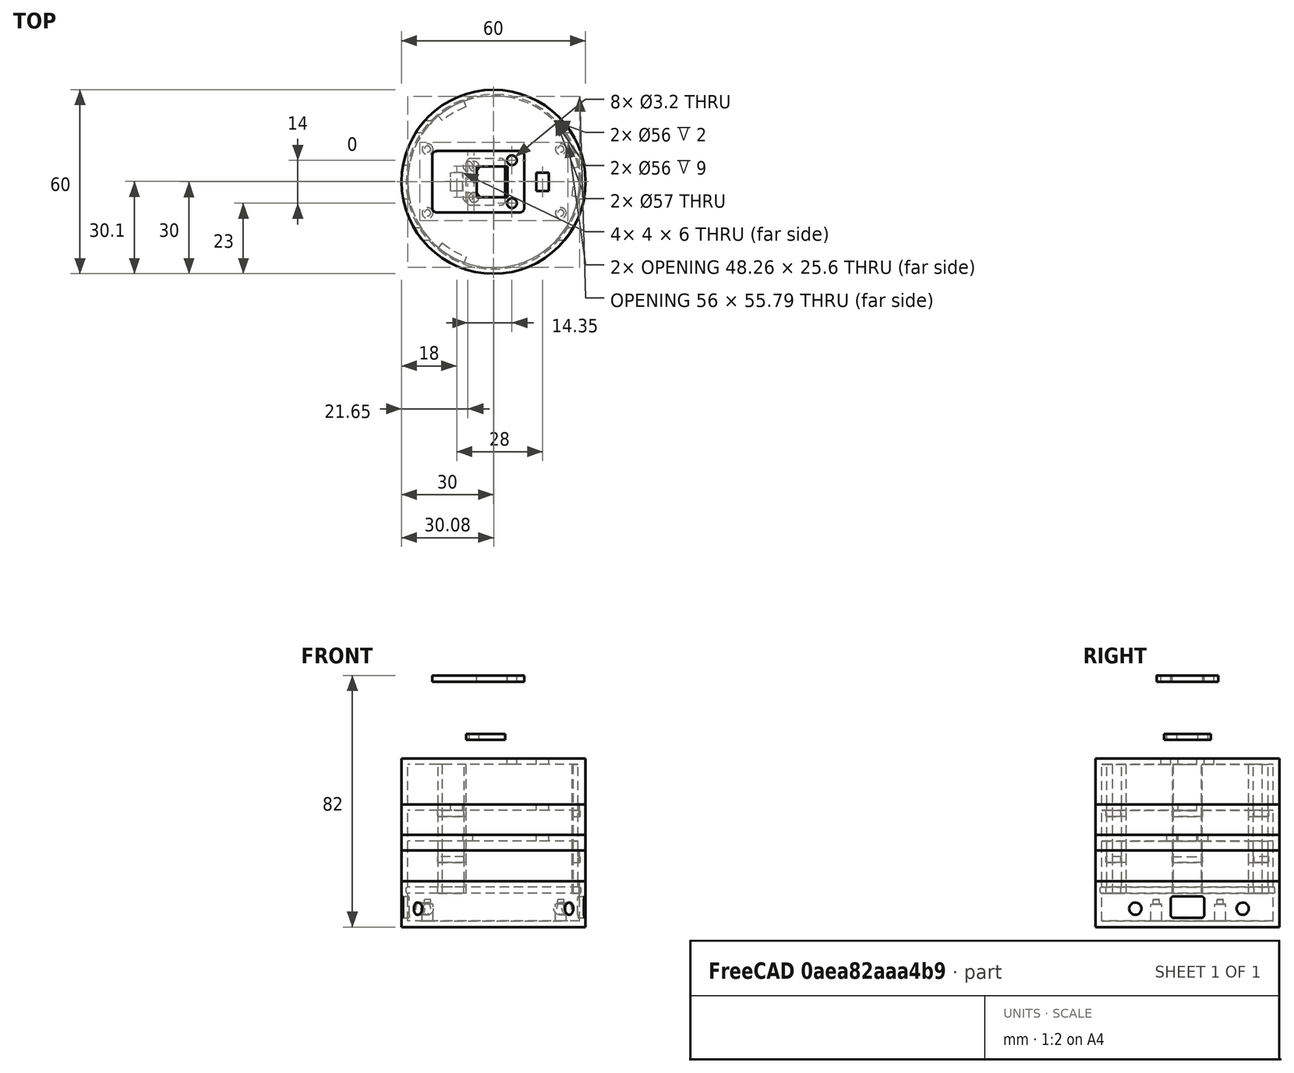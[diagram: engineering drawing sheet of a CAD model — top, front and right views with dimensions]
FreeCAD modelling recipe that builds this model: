
FCSTD DOCUMENT  (FreeCAD 0.18R16146 (Git))
Label: Esp8266_NodeMCU_SensorHousing
License: All rights reserved
LicenseURL: http://en.wikipedia.org/wiki/All_rights_reserved
objects: Part::Cylinder×19, Part::Cut×18, Part::Box×10, Part::MultiFuse×10, Part::Fillet×6, Part::Fuse×4, App::DocumentObjectGroup×3
note: 67 computed .brp shape members not serialized (recipe doc carries the construction recipe); baked Part::Feature solids carry a one-line shape summary decoded from their .brp

FEATURE [Part::Box] Box  label="ESP8266MountingBlock"
  AttacherType = Attacher::AttachEngine3D
  Height = 2
  Length = 48.26
  Width = 25.6
FEATURE [Part::Cylinder] Cylinder  label="DistancePieceLowerLeft"
  Angle = 360
  AttacherType = Attacher::AttachEngine3D
  Height = 7.5
  Placement = pos=(2.54,2.54,0) rot=(0,0,1;0rad)
  Radius = 1.75
FEATURE [Part::Cylinder] Cylinder001  label="MountPieceLowerLeft"
  Angle = 360
  AttacherType = Attacher::AttachEngine3D
  Height = 9
  Placement = pos=(2.54,2.54,0) rot=(0,0,1;0rad)
  Radius = 1
FEATURE [Part::Fuse] Fusion  label="LowerLeftMount"
  Base = -> Cylinder
  Tool = -> Cylinder001
FEATURE [Part::Fuse] Fusion001  label="LowerRightMount"
  Base = -> Cylinder
  Placement = pos=(43.434,0,0) rot=(0,0,1;0rad)
  Tool = -> Cylinder001
FEATURE [Part::Fuse] Fusion002  label="UpperLeftMount"
  Base = -> Cylinder
  Placement = pos=(0,20.828,0) rot=(0,0,1;0rad)
  Tool = -> Cylinder001
FEATURE [Part::Fuse] Fusion003  label="UpperRightMount"
  Base = -> Cylinder
  Placement = pos=(43.434,20.828,0) rot=(0,0,1;0rad)
  Tool = -> Cylinder001
FEATURE [Part::Fillet] Fillet
  Base = -> Box
  Edges = 4 edges r=2: [Edge1,Edge3,Edge5,Edge7]
FEATURE [Part::MultiFuse] Fusion004  label="ESP8266_bracket"
  Placement = pos=(-24.05,-12.7,0) rot=(0,0,1;0rad)
  Shapes = -> [Fusion002,Fusion003,Fillet,Fusion001,Fusion]
FEATURE [Part::Cylinder] Cylinder002  label="LowerHousingOuter"
  Angle = 360
  AttacherType = Attacher::AttachEngine3D
  Height = 15
  Radius = 30
FEATURE [Part::Cylinder] Cylinder003  label="LowerHousingInner"
  Angle = 360
  AttacherType = Attacher::AttachEngine3D
  Height = 15
  Placement = pos=(0,0,2) rot=(0,0,1;0rad)
  Radius = 28
FEATURE [Part::Cut] Cut  label="LowerHousing"
  Base = -> Cylinder002
  Tool = -> Cylinder003
FEATURE [Part::Cylinder] Cylinder004  label="UpperHousingOuter"
  Angle = 360
  AttacherType = Attacher::AttachEngine3D
  Height = 15
  Placement = pos=(0,0,15) rot=(0,0,1;0rad)
  Radius = 30
FEATURE [Part::Cylinder] Cylinder005  label="UpperHousingInner"
  Angle = 360
  AttacherType = Attacher::AttachEngine3D
  Height = 13
  Placement = pos=(0,0,15) rot=(0,0,1;0rad)
  Radius = 28
FEATURE [Part::Cylinder] Cylinder006  label="LowerHousingNotch"
  Angle = 360
  AttacherType = Attacher::AttachEngine3D
  Height = 2
  Placement = pos=(0,0,11) rot=(0,0,1;0rad)
  Radius = 28.5
FEATURE [Part::Cut] Cut002  label="UpperHousing"
  Base = -> Cylinder004
  Tool = -> Cylinder005
FEATURE [Part::Cylinder] Cylinder007  label="UpperHousingCatchOuter"
  Angle = 360
  AttacherType = Attacher::AttachEngine3D
  Height = 17
  Placement = pos=(0,0,11) rot=(0,0,1;0rad)
  Radius = 28
FEATURE [Part::Cylinder] Cylinder008  label="UpperHousingCatch"
  Angle = 360
  AttacherType = Attacher::AttachEngine3D
  Height = 2
  Placement = pos=(0,0,11) rot=(0,0,1;0rad)
  Radius = 28.3
FEATURE [Part::Cylinder] Cylinder009  label="UpperHousingCatchInner"
  Angle = 360
  AttacherType = Attacher::AttachEngine3D
  Height = 17
  Placement = pos=(0,0,11) rot=(0,0,1;0rad)
  Radius = 26
FEATURE [Part::Fillet] Fillet001  label="LowerHousingNotchFillet"
  Base = -> Cylinder006
  Edges = 2 edges r=0.5: [Edge1,Edge3]
FEATURE [Part::Cut] Cut004  label="LowerHousingWithNotch"
  Base = -> Cut
  Tool = -> Fillet001
FEATURE [Part::Fillet] Fillet002
  Base = -> Cylinder008
  Edges = 2 edges r=0.4: [Edge1,Edge3]
FEATURE [Part::MultiFuse] Fusion005
  Shapes = -> [Fillet002,Cylinder007]
FEATURE [Part::Cut] Cut005  label="UpperHousingCompleteCatchCut"
  Base = -> Fusion005
  Tool = -> Cylinder009
FEATURE [Part::Box] Box003  label="DHT22PCB"
  AttacherType = Attacher::AttachEngine3D
  Height = 2
  Length = 30
  Placement = pos=(-20,-10,0) rot=(0,0,1;0rad)
  Width = 20
FEATURE [Part::Cylinder] Cylinder010  label="DHT22PCBMountingLeft"
  Angle = 360
  AttacherType = Attacher::AttachEngine3D
  Height = 10
  Placement = pos=(6,-7,-8) rot=(0,0,1;0rad)
  Radius = 1.6
FEATURE [Part::Cylinder] Cylinder011  label="DHT22PCBMountingRight"
  Angle = 360
  AttacherType = Attacher::AttachEngine3D
  Height = 10
  Placement = pos=(6,7,-8) rot=(0,0,1;0rad)
  Radius = 1.6
FEATURE [Part::Box] Box004  label="DHT22CableHole"
  AttacherType = Attacher::AttachEngine3D
  Height = 10
  Length = 4
  Placement = pos=(14,-3,-8) rot=(0,0,1;0rad)
  Width = 6
FEATURE [Part::Cylinder] Cylinder012  label="UpperHousingCatchCut1"
  Angle = 100
  AttacherType = Attacher::AttachEngine3D
  Height = 28
  Placement = pos=(0,0,0) rot=(0,0,1;0.174533rad)
  Radius = 30
FEATURE [Part::Cylinder] Cylinder013  label="UpperHousingCatchCut2"
  Angle = 100
  AttacherType = Attacher::AttachEngine3D
  Height = 28
  Placement = pos=(0,0,0) rot=(0,0,1;2.26893rad)
  Radius = 30
FEATURE [Part::Cylinder] Cylinder014  label="UpperHousingCatchCut3"
  Angle = 100
  AttacherType = Attacher::AttachEngine3D
  Height = 28
  Placement = pos=(0,0,0) rot=(0,0,-1;1.91986rad)
  Radius = 30
FEATURE [Part::Cut] Cut006  label="UpperHousingSmallCatchCut1"
  Base = -> Cut005
  Tool = -> Cylinder012
FEATURE [Part::Cut] Cut007  label="UpperHousingSmallCatchCut2"
  Base = -> Cut006
  Tool = -> Cylinder013
FEATURE [Part::Cut] Cut008  label="UpperHousingSmallCatch"
  Base = -> Cut007
  Tool = -> Cylinder014
FEATURE [Part::MultiFuse] Fusion008  label="UpperHousingWithCatch"
  Shapes = -> [Cut002,Cut008]
FEATURE [Part::Cylinder] Cylinder015  label="LeftHole"
  Angle = 360
  AttacherType = Attacher::AttachEngine3D
  Height = 60
  Placement = pos=(-30,-17,6) rot=(0,1,0;1.5708rad)
  Radius = 2
FEATURE [Part::Cylinder] Cylinder016  label="RightHole"
  Angle = 360
  AttacherType = Attacher::AttachEngine3D
  Height = 60
  Placement = pos=(-30,18,6) rot=(0,1,0;1.5708rad)
  Radius = 2
FEATURE [Part::Cut] Cut010  label="LowerHousingWithNotchRightHoleCut"
  Base = -> Cut004
  Tool = -> Cylinder016
FEATURE [Part::Cut] Cut011  label="LowerHousingWithNotchAndHoles"
  Base = -> Cut010
  Tool = -> Cylinder015
FEATURE [Part::MultiFuse] Fusion009  label="LowerHousingWithBracket"
  Shapes = -> [Cut011,Fusion004]
FEATURE [Part::MultiFuse] Fusion011  label="DHT22"
  Shapes = -> [Box003,Cylinder010,Cylinder011]
FEATURE [Part::MultiFuse] Fusion012  label="DHT22WithCableHole"
  Placement = pos=(0,0,30) rot=(0,0,1;0rad)
  Shapes = -> [Fusion011,Box004]
FEATURE [Part::Cut] Cut012  label="UpperHousingDHT22"
  Base = -> Fusion008
  Placement = pos=(0,0,25) rot=(0,0,1;0rad)
  Tool = -> Fusion012
FEATURE [Part::Cut] Cut013  label="DHT22LeftMountCut"
  Base = -> Box003
  Tool = -> Cylinder010
FEATURE [Part::Cut] Cut014  label="DHT22RightMountCut"
  Base = -> Cut013
  Tool = -> Cylinder011
FEATURE [Part::Fillet] Fillet003
  Base = -> Cut014
  Edges = 4 edges r=1.5: [Edge1,Edge3,Edge6,Edge13]
FEATURE [Part::Box] Box005  label="DHT22PinCut"
  AttacherType = Attacher::AttachEngine3D
  Height = 10
  Length = 10
  Placement = pos=(-5.5,-5,0) rot=(0,0,1;0rad)
  Width = 10
FEATURE [Part::Cut] Cut015  label="DHT22Spacer"
  Base = -> Fillet003
  Placement = pos=(0,0,80) rot=(0,0,1;0rad)
  Tool = -> Box005
FEATURE [Part::Box] Box006  label="Si7021PCB"
  AttacherType = Attacher::AttachEngine3D
  Height = 2
  Length = 17.78
  Placement = pos=(-8.89,-7.62,0) rot=(0,0,1;0rad)
  Width = 15.24
FEATURE [Part::Cylinder] Cylinder017  label="Si7021PCBMountingLeft"
  Angle = 360
  AttacherType = Attacher::AttachEngine3D
  Height = 10
  Placement = pos=(-6.35,5.08,-8) rot=(0,0,1;0rad)
  Radius = 1.6
FEATURE [Part::Cylinder] Cylinder018  label="Si7021PCBMountingRight"
  Angle = 360
  AttacherType = Attacher::AttachEngine3D
  Height = 10
  Placement = pos=(-6.35,-5.08,-8) rot=(0,0,1;0rad)
  Radius = 1.6
FEATURE [Part::Box] Box007  label="Si7021CableHole"
  AttacherType = Attacher::AttachEngine3D
  Height = 10
  Length = 4
  Placement = pos=(14,-3,-8) rot=(0,0,1;0rad)
  Width = 6
FEATURE [Part::MultiFuse] Fusion013  label="Si7021"
  Placement = pos=(-2,0,0) rot=(0,0,1;0rad)
  Shapes = -> [Box006,Cylinder018,Cylinder017]
FEATURE [Part::MultiFuse] Fusion014  label="Si7021WithCableHole"
  Placement = pos=(0,0,30) rot=(0,0,1;0rad)
  Shapes = -> [Fusion013,Box007]
FEATURE [Part::Cut] Cut016  label="UpperHousingSi7021"
  Base = -> Fusion008
  Tool = -> Fusion014
FEATURE [Part::Box] Box008  label="Si7021PCBShort"
  AttacherType = Attacher::AttachEngine3D
  Height = 2
  Length = 12.7
  Placement = pos=(-8.89,-7.62,0) rot=(0,0,1;0rad)
  Width = 15.24
FEATURE [Part::Cut] Cut017  label="Si7021PCBMountingRight001"
  Base = -> Box008
  Tool = -> Cylinder018
FEATURE [Part::Cut] Cut018  label="Si7021PCBMountingLeft001"
  Base = -> Cut017
  Tool = -> Cylinder017
FEATURE [Part::Fillet] Fillet004  label="Si7021Spacer"
  Base = -> Cut018
  Edges = 4 edges r=1.5: [Edge1,Edge3,Edge6,Edge13]
  Placement = pos=(0,0,61) rot=(0,0,1;0rad)
FEATURE [App::DocumentObjectGroup] Gruppe  label="DHT023"
  Group = -> [Cut015,Cut012]
FEATURE [App::DocumentObjectGroup] Gruppe001  label="Si7023"
  Group = -> [Cut016,Fillet004]
FEATURE [Part::Box] Box009  label="NoSensorCableHole1"
  AttacherType = Attacher::AttachEngine3D
  Height = 10
  Length = 4
  Placement = pos=(14,-3,-8) rot=(0,0,1;0rad)
  Width = 6
FEATURE [Part::Box] Box010  label="NoSensorCableHole2"
  AttacherType = Attacher::AttachEngine3D
  Height = 10
  Length = 4
  Placement = pos=(-14,-3,-8) rot=(0,0,1;0rad)
  Width = 6
FEATURE [Part::MultiFuse] Fusion015  label="NoSensorCableHole"
  Placement = pos=(0,0,30) rot=(0,0,1;0rad)
  Shapes = -> [Box009,Box010]
FEATURE [Part::Cut] Cut019  label="UpperHousingNoSensor"
  Base = -> Fusion008
  Placement = pos=(0,0,10) rot=(0,0,1;0rad)
  Tool = -> Fusion015
FEATURE [App::DocumentObjectGroup] Gruppe002  label="NoSensor"
  Group = -> [Cut019]
FEATURE [Part::Box] Box011  label="USBHole"
  AttacherType = Attacher::AttachEngine3D
  Height = 7
  Length = 60
  Placement = pos=(-30,-5.5,3) rot=(0,0,1;0rad)
  Width = 11
FEATURE [Part::Fillet] Fillet005  label="USBHoleCutout"
  Base = -> Box011
  Edges = 4 edges r=1: [Edge9,Edge10,Edge11,Edge12]
FEATURE [Part::Cut] Cut020  label="LowerHousingWithNotchUSBCut"
  Base = -> Cut004
  Tool = -> Fillet005
FEATURE [Part::MultiFuse] Fusion016  label="LowerHousingWithBracketUSB"
  Shapes = -> [Fusion004,Cut020]
